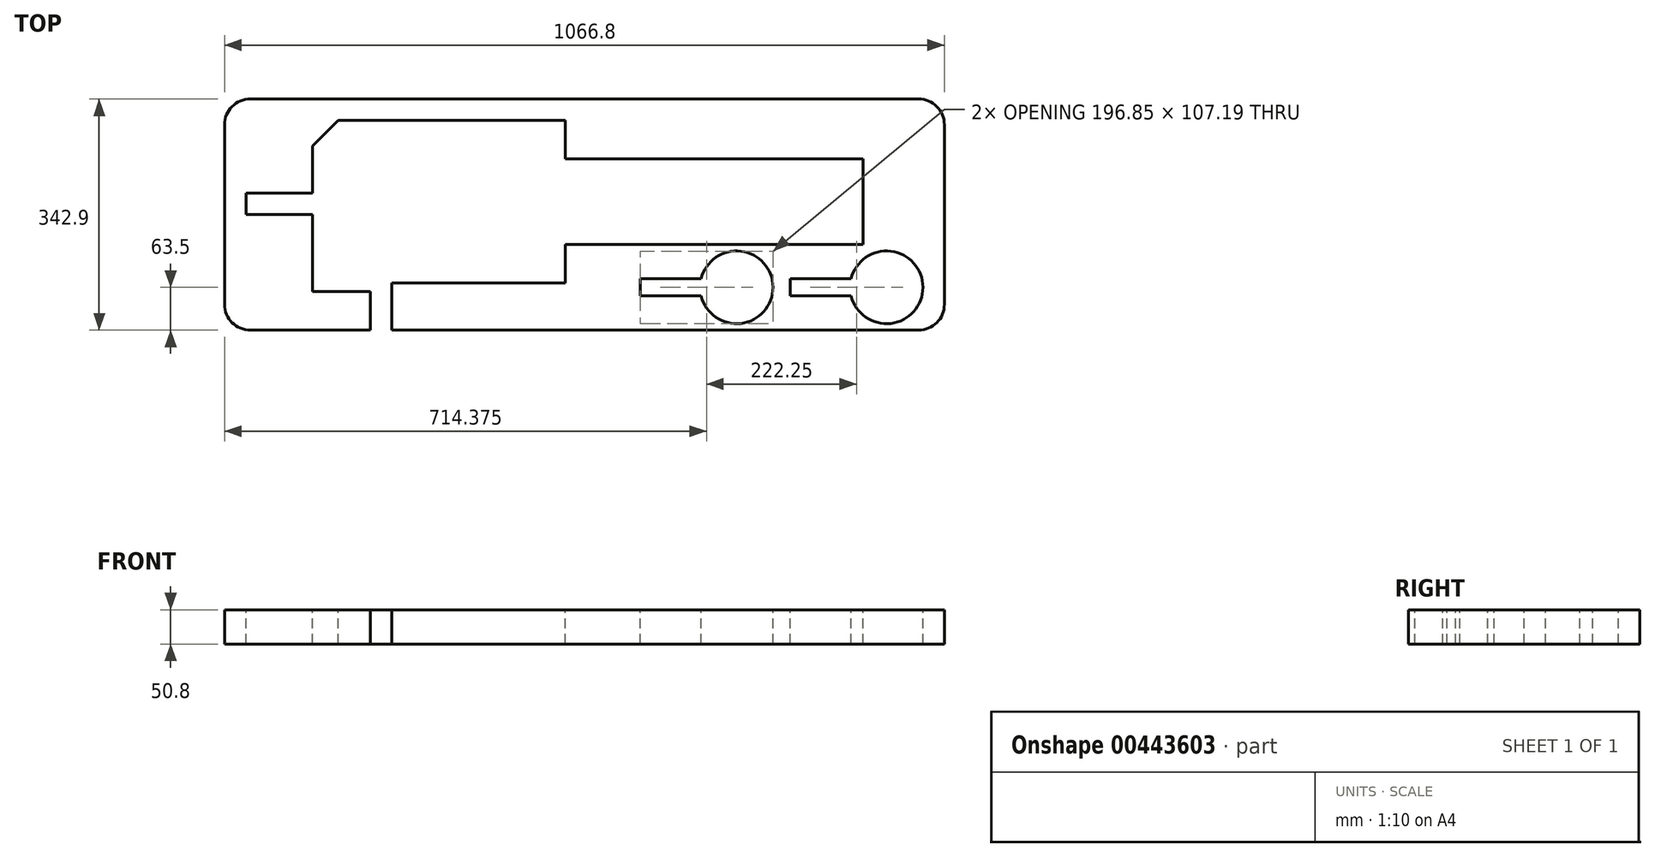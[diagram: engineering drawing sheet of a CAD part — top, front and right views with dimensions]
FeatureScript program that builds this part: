
annotation { "Feature Type Name" : "Feature", "Feature Type Description" : "" }
export const myFeature = defineFeature(function(context is Context, id is Id, definition is map)
    precondition{}
    {
        {
            var Q0;
            Q0=qCreatedBy(makeId("Top.planeOp"),FACE);
            var sketch = newSketch(context, id + "F0", { "sketchPlane" : qUnion([Q0])});
            skLineSegment(sketch, "E0.bottom", {"start": v(533.4, -171.45) * mm, "end": v(-533.4, -171.45) * mm});
            skLineSegment(sketch, "E0.top", {"start": v(533.4, 171.45) * mm, "end": v(-533.4, 171.45) * mm});
            skLineSegment(sketch, "E0.left", {"start": v(533.4, -171.45) * mm, "end": v(533.4, 171.45) * mm});
            skLineSegment(sketch, "E0.right", {"start": v(-533.4, -171.45) * mm, "end": v(-533.4, 171.45) * mm});
            skPoint(sketch, "E0.middle", {"position": v(0, 0) * mm});
            skSolve(sketch);
        }
        {
            var Q0;
            Q0 = qSketchRegion(id + "F0", true);
            extrude(context, id + "F1", {"entities" : qUnion([Q0]), "depth" : 50.8 * mm});
        }
        {
            var Q0;
            Q0=makeQuery(id+"F1.opExtrude","CAP_FACE",FACE,{"disambiguationData":[OSD([sQuery(id+"F0.wireOp",EDGE,"E0.bottom"),sQuery(id+"F0.wireOp",EDGE,"E0.top"),sQuery(id+"F0.wireOp",EDGE,"E0.left"),sQuery(id+"F0.wireOp",EDGE,"E0.right")])],"isStart":false});
            var sketch = newSketch(context, id + "F2", { "sketchPlane" : qUnion([Q0])});
            skLineSegment(sketch, "E1", {"start": v(-317.5, -171.45) * mm, "end": v(-285.75, -171.45) * mm});
            skLineSegment(sketch, "E2", {"start": v(412.75, 82.55) * mm, "end": v(-28.57, 82.55) * mm});
            skLineSegment(sketch, "E3", {"start": v(-28.57, 82.55) * mm, "end": v(-28.57, 139.7) * mm});
            skLineSegment(sketch, "E4", {"start": v(-317.5, -171.45) * mm, "end": v(-317.5, -114.3) * mm});
            skLineSegment(sketch, "E5", {"start": v(-285.75, -171.45) * mm, "end": v(-285.75, -101.6) * mm});
            skLineSegment(sketch, "E6", {"start": v(-285.75, -101.6) * mm, "end": v(-28.57, -101.6) * mm});
            skLineSegment(sketch, "E7", {"start": v(-28.57, -101.6) * mm, "end": v(-28.57, -44.45) * mm});
            skLineSegment(sketch, "E8", {"start": v(-28.57, -44.45) * mm, "end": v(412.75, -44.45) * mm});
            skLineSegment(sketch, "E9", {"start": v(412.75, -44.45) * mm, "end": v(412.75, 82.55) * mm});
            skLineSegment(sketch, "E10", {"start": v(-403.23, 101.54) * mm, "end": v(-403.23, 31.75) * mm});
            skLineSegment(sketch, "E11", {"start": v(-403.23, 31.75) * mm, "end": v(-501.65, 31.75) * mm});
            skLineSegment(sketch, "E12", {"start": v(-501.65, 31.75) * mm, "end": v(-501.65, 0) * mm});
            skLineSegment(sketch, "E13", {"start": v(-501.65, 0) * mm, "end": v(-403.23, 0) * mm});
            skLineSegment(sketch, "E14", {"start": v(-403.23, 0) * mm, "end": v(-403.23, -114.3) * mm});
            skLineSegment(sketch, "E15", {"start": v(-403.22, -114.3) * mm, "end": v(-317.5, -114.3) * mm});
            skLineSegment(sketch, "E16", {"start": v(-28.57, 139.7) * mm, "end": v(-365.13, 139.7) * mm});
            skLineSegment(sketch, "E17", {"start": v(-365.13, 139.7) * mm, "end": v(-403.23, 101.54) * mm});
            skSolve(sketch);
        }
        {
            var Q0;
            Q0 = qSketchRegion(id + "F2", true);
            extrude(context, id + "F3", {"entities" : qUnion([Q0]), "operationType" : NewBodyOperationType.REMOVE, "oppositeDirection" : true, "depth" : 50.8 * mm});
        }
        {
            var Q0;
            Q0=makeQuery(id+"F1.opExtrude","SWEPT_EDGE",EDGE,{"disambiguationData":[OSD([sQuery(id+"F0.wireOp",EDGE,"E0.top"),sQuery(id+"F0.wireOp",EDGE,"E0.right")])]});
            var Q1;
            Q1=makeQuery(id+"F1.opExtrude","SWEPT_EDGE",EDGE,{"disambiguationData":[OSD([sQuery(id+"F0.wireOp",EDGE,"E0.bottom"),sQuery(id+"F0.wireOp",EDGE,"E0.right")])]});
            var Q2;
            Q2=makeQuery(id+"F1.opExtrude","SWEPT_EDGE",EDGE,{"disambiguationData":[OSD([sQuery(id+"F0.wireOp",EDGE,"E0.top"),sQuery(id+"F0.wireOp",EDGE,"E0.left")])]});
            var Q3;
            Q3=makeQuery(id+"F1.opExtrude","SWEPT_EDGE",EDGE,{"disambiguationData":[OSD([sQuery(id+"F0.wireOp",EDGE,"E0.bottom"),sQuery(id+"F0.wireOp",EDGE,"E0.left")])]});
            fillet(context, id + "F4", {"entities" : qUnion([Q0, Q1, Q2, Q3]), "radius" : 38.1 * mm, "tangentPropagation" : true, "allowEdgeOverflow" : false});
        }
        {
            var Q0;
            Q0=makeQuery(id+"F1.opExtrude","CAP_FACE",FACE,{"disambiguationData":[OSD([sQuery(id+"F0.wireOp",EDGE,"E0.bottom"),sQuery(id+"F0.wireOp",EDGE,"E0.top"),sQuery(id+"F0.wireOp",EDGE,"E0.left"),sQuery(id+"F0.wireOp",EDGE,"E0.right")])],"isStart":false});
            var sketch = newSketch(context, id + "F5", { "sketchPlane" : qUnion([Q0])});
            skLineSegment(sketch, "E18", {"start": v(82.55, -95.25) * mm, "end": v(82.55, -120.65) * mm});
            skCircle(sketch, "E19", {"center": v(225.43, -107.95) * mm, "radius": 53.97 * mm});
            skPoint(sketch, "E19.centerSnap0", {"position": v(82.55, -107.95) * mm});
            skLineSegment(sketch, "E20", {"start": v(82.55, -95.25) * mm, "end": v(172.97, -95.25) * mm});
            skLineSegment(sketch, "E21", {"start": v(82.55, -120.65) * mm, "end": v(172.97, -120.65) * mm});
            skSolve(sketch);
        }
        {
            var Q0;
            Q0 = qSketchRegion(id + "F5", true);
            extrude(context, id + "F6", {"entities" : qUnion([Q0]), "operationType" : NewBodyOperationType.REMOVE, "oppositeDirection" : true, "depth" : 50.8 * mm});
        }
        {
            var Q0;
            Q0=makeQuery(id+"F1.opExtrude","CAP_FACE",FACE,{"disambiguationData":[OSD([sQuery(id+"F0.wireOp",EDGE,"E0.bottom"),sQuery(id+"F0.wireOp",EDGE,"E0.top"),sQuery(id+"F0.wireOp",EDGE,"E0.left"),sQuery(id+"F0.wireOp",EDGE,"E0.right")])],"isStart":false});
            var sketch = newSketch(context, id + "F7", { "sketchPlane" : qUnion([Q0])});
            skLineSegment(sketch, "E22", {"start": v(304.8, -95.25) * mm, "end": v(304.8, -120.65) * mm});
            skCircle(sketch, "E23", {"center": v(447.68, -107.95) * mm, "radius": 53.97 * mm});
            skPoint(sketch, "E23.centerSnap0", {"position": v(304.8, -107.95) * mm});
            skLineSegment(sketch, "E24", {"start": v(304.8, -95.25) * mm, "end": v(395.22, -95.25) * mm});
            skLineSegment(sketch, "E25", {"start": v(304.8, -120.65) * mm, "end": v(395.22, -120.65) * mm});
            skSolve(sketch);
        }
        {
            var Q0;
            Q0 = qSketchRegion(id + "F7", true);
            extrude(context, id + "F8", {"entities" : qUnion([Q0]), "operationType" : NewBodyOperationType.REMOVE, "oppositeDirection" : true, "depth" : 50.8 * mm});
        }
    });
